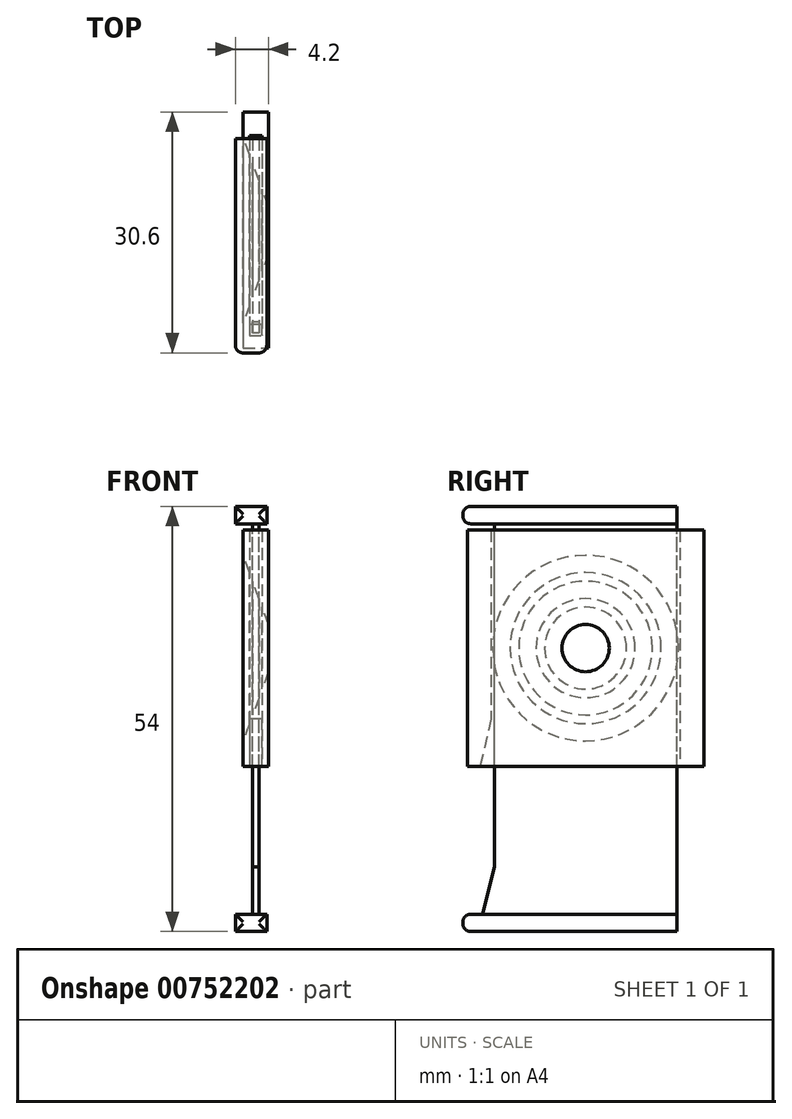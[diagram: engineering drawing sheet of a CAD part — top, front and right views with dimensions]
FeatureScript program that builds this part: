
annotation { "Feature Type Name" : "Feature", "Feature Type Description" : "" }
export const myFeature = defineFeature(function(context is Context, id is Id, definition is map)
    precondition{}
    {
        {
            var Q0;
            Q0=qCreatedBy(makeId("Top.planeOp"),FACE);
            var sketch = newSketch(context, id + "F0", { "sketchPlane" : qUnion([Q0])});
            skLineSegment(sketch, "E0.bottom", {"start": v(0, 15) * mm, "end": v(0.8, 15) * mm});
            skLineSegment(sketch, "E0.top", {"start": v(0, -15) * mm, "end": v(0.8, -15) * mm});
            skLineSegment(sketch, "E0.left", {"start": v(0, 15) * mm, "end": v(0, -15) * mm});
            skLineSegment(sketch, "E0.right", {"start": v(0.8, 15) * mm, "end": v(0.8, -15) * mm});
            skLineSegment(sketch, "E1.bottom", {"start": v(0.8, 15) * mm, "end": v(2.4, 15) * mm});
            skLineSegment(sketch, "E1.top", {"start": v(0.8, 12) * mm, "end": v(2.4, 12) * mm});
            skLineSegment(sketch, "E1.left", {"start": v(0.8, 15) * mm, "end": v(0.8, 12) * mm});
            skLineSegment(sketch, "E1.right", {"start": v(2.4, 15) * mm, "end": v(2.4, 12) * mm});
            skLineSegment(sketch, "E2.bottom", {"start": v(0.8, -15) * mm, "end": v(2.4, -15) * mm});
            skLineSegment(sketch, "E2.top", {"start": v(0.8, -12) * mm, "end": v(2.4, -12) * mm});
            skLineSegment(sketch, "E2.left", {"start": v(0.8, -15) * mm, "end": v(0.8, -12) * mm});
            skLineSegment(sketch, "E2.right", {"start": v(2.4, -15) * mm, "end": v(2.4, -12) * mm});
            skLineSegment(sketch, "E3.bottom", {"start": v(2.4, 15) * mm, "end": v(3.2, 15) * mm});
            skLineSegment(sketch, "E3.top", {"start": v(2.4, -15) * mm, "end": v(3.2, -15) * mm});
            skLineSegment(sketch, "E3.left", {"start": v(2.4, 15) * mm, "end": v(2.4, -15) * mm});
            skLineSegment(sketch, "E3.right", {"start": v(3.2, 15) * mm, "end": v(3.2, -15) * mm});
            skLineSegment(sketch, "E4.left", {"start": v(2.4, -15) * mm, "end": v(2.4, -15) * mm});
            skLineSegment(sketch, "E4.right", {"start": v(3.2, -15) * mm, "end": v(3.2, -15) * mm});
            skSolve(sketch);
        }
        {
            var Q0;
            Q0=makeQuery(id+"F0.imprint","IMPRINT",FACE,{"disambiguationData":[TD([[makeQuery(id+"F0.imprint","IMPRINT",EDGE,{"derivedFrom":sQuery(id+"F0.wireOp",EDGE,"E0.right")}),-1.0]])]});
            var Q1;
            {var subQ0=sQuery(id+"F0.wireOp",EDGE,"E1.bottom");Q1=makeQuery(id+"F0.imprint","IMPRINT",FACE,{"disambiguationData":[TD([[makeQuery(id+"F0.imprint","IMPRINT",EDGE,{"derivedFrom":subQ0}),-1.0]])]});}
            var Q2;
            {var subQ4=sQuery(id+"F0.wireOp",EDGE,"E3.bottom");Q2=makeQuery(id+"F0.imprint","IMPRINT",FACE,{"disambiguationData":[TD([[makeQuery(id+"F0.imprint","IMPRINT",EDGE,{"derivedFrom":subQ4}),-1.0]])]});}
            var Q3;
            {var subQ0=sQuery(id+"F0.wireOp",EDGE,"E2.bottom");Q3=makeQuery(id+"F0.imprint","IMPRINT",FACE,{"disambiguationData":[TD([[makeQuery(id+"F0.imprint","IMPRINT",EDGE,{"derivedFrom":subQ0}),1.0]])]});}
            var Q4;
            {var subQ0=sQuery(id+"F0.wireOp",EDGE,"E0.left");Q4=makeQuery(id+"F0.imprint","IMPRINT",FACE,{"disambiguationData":[TD([[makeQuery(id+"F0.imprint","IMPRINT",EDGE,{"derivedFrom":subQ0}),1.0]])]});}
            extrude(context, id + "F1", {"entities" : qUnion([Q0, Q1, Q2, Q3, Q4]), "endBound" : BoundingType.SYMMETRIC, "depth" : 30 * mm, "offsetDistance" : 25 * mm});
        }
        {
            var Q0;
            Q0=makeQuery(id+"F1.opExtrude","CAP_FACE",FACE,{"disambiguationData":[OSD([sQuery(id+"F0.wireOp",EDGE,"E0.bottom"),sQuery(id+"F0.wireOp",EDGE,"E0.top"),sQuery(id+"F0.wireOp",EDGE,"E0.left"),sQuery(id+"F0.wireOp",EDGE,"E0.right"),sQuery(id+"F0.wireOp",EDGE,"E1.bottom"),sQuery(id+"F0.wireOp",EDGE,"E1.top"),sQuery(id+"F0.wireOp",EDGE,"E2.bottom"),sQuery(id+"F0.wireOp",EDGE,"E2.top"),sQuery(id+"F0.wireOp",EDGE,"E3.bottom"),sQuery(id+"F0.wireOp",EDGE,"E3.left"),sQuery(id+"F0.wireOp",EDGE,"E3.right"),sQuery(id+"F0.wireOp",EDGE,"E3.top")])],"isStart":false});
            var sketch = newSketch(context, id + "F2", { "sketchPlane" : qUnion([Q0])});
            skLineSegment(sketch, "E5.bottom", {"start": v(1.2, 11.6) * mm, "end": v(2, 11.6) * mm});
            skLineSegment(sketch, "E5.top", {"start": v(1.2, -11.6) * mm, "end": v(2, -11.6) * mm});
            skLineSegment(sketch, "E5.left", {"start": v(1.2, 11.6) * mm, "end": v(1.2, -11.6) * mm});
            skLineSegment(sketch, "E5.right", {"start": v(2, 11.6) * mm, "end": v(2, -11.6) * mm});
            skSolve(sketch);
        }
        {
            var Q0;
            Q0=makeQuery(id+"F2.imprint","IMPRINT",FACE,{"disambiguationData":[TD([[makeQuery(id+"F2.imprint","IMPRINT",EDGE,{"derivedFrom":sQuery(id+"F2.wireOp",EDGE,"E5.bottom")}),-1.0]])]});
            extrude(context, id + "F3", {"entities" : qUnion([Q0]), "oppositeDirection" : true, "depth" : 50 * mm, "offsetDistance" : 25 * mm, "hasSecondDirection" : true, "secondDirectionOppositeDirection" : false, "secondDirectionDepth" : 2 * mm});
        }
        {
            var Q0;
            Q0=makeQuery(id+"F1.opExtrude","SWEPT_FACE",FACE,{"disambiguationData":[OSD([sQuery(id+"F0.wireOp",EDGE,"E3.right")])]});
            var sketch = newSketch(context, id + "F4", { "sketchPlane" : qUnion([Q0])});
            skCircle(sketch, "E6", {"center": v(0, 0) * mm, "radius": 3 * mm});
            skSolve(sketch);
        }
        {
            var Q0;
            Q0=qSketchRegion(id+"F4",true);
            extrude(context, id + "F5", {"entities" : qUnion([Q0]), "operationType" : NewBodyOperationType.REMOVE, "oppositeDirection" : true, "depth" : 25 * mm, "offsetDistance" : 25 * mm, "hasDraft" : true, "draftAngle" : 70 * degree});
        }
        {
            var Q0;
            Q0=makeQuery(id+"F3.opExtrude","SWEPT_FACE",FACE,{"disambiguationData":[OSD([sQuery(id+"F2.wireOp",EDGE,"E5.right")])]});
            var sketch = newSketch(context, id + "F6", { "sketchPlane" : qUnion([Q0])});
            skLineSegment(sketch, "E7.bottom", {"start": v(11.6, 17) * mm, "end": v(-15.6, 17) * mm});
            skLineSegment(sketch, "E7.top", {"start": v(11.6, 15.8) * mm, "end": v(-15.6, 15.8) * mm});
            skLineSegment(sketch, "E7.left", {"start": v(11.6, 17) * mm, "end": v(11.6, 15.8) * mm});
            skLineSegment(sketch, "E7.right", {"start": v(-15.6, 17) * mm, "end": v(-15.6, 15.8) * mm});
            skLineSegment(sketch, "E8.bottom", {"start": v(11.6, -35) * mm, "end": v(-15.6, -35) * mm});
            skLineSegment(sketch, "E8.top", {"start": v(11.6, -33.8) * mm, "end": v(-15.6, -33.8) * mm});
            skLineSegment(sketch, "E8.left", {"start": v(11.6, -35) * mm, "end": v(11.6, -33.8) * mm});
            skLineSegment(sketch, "E8.right", {"start": v(-15.6, -35) * mm, "end": v(-15.6, -33.8) * mm});
            skLineSegment(sketch, "E9.top", {"start": v(11.6, 18) * mm, "end": v(-15.6, 18) * mm});
            skLineSegment(sketch, "E9.left", {"start": v(11.6, 17) * mm, "end": v(11.6, 18) * mm});
            skLineSegment(sketch, "E9.right", {"start": v(-15.6, 17) * mm, "end": v(-15.6, 18) * mm});
            skLineSegment(sketch, "E10.top", {"start": v(11.6, -36) * mm, "end": v(-15.6, -36) * mm});
            skLineSegment(sketch, "E10.left", {"start": v(11.6, -35) * mm, "end": v(11.6, -36) * mm});
            skLineSegment(sketch, "E10.right", {"start": v(-15.6, -35) * mm, "end": v(-15.6, -36) * mm});
            skSolve(sketch);
        }
        {
            var Q0;
            Q0=qSketchRegion(id+"F6",true);
            extrude(context, id + "F7", {"entities" : qUnion([Q0]), "operationType" : NewBodyOperationType.ADD, "depth" : 1 * mm, "offsetDistance" : 25 * mm, "hasSecondDirection" : true, "secondDirectionOppositeDirection" : true, "secondDirectionDepth" : 3 * mm});
        }
        {
            var Q0;
            Q0=makeQuery(id+"F7.opExtrude","SWEPT_FACE",FACE,{"disambiguationData":[OSD([sQuery(id+"F6.wireOp",EDGE,"E8.right")])]});
            var Q1;
            Q1=makeQuery(id+"F7.opExtrude","SWEPT_FACE",FACE,{"disambiguationData":[OSD([sQuery(id+"F6.wireOp",EDGE,"E7.right")])]});
            fillet(context, id + "F8", {"entities" : qUnion([Q0, Q1]), "radius" : 1 * mm, "tangentPropagation" : true, "allowEdgeOverflow" : false});
        }
        {
            var Q0;
            Q0=makeQuery(id+"F7.boolean.opBoolean","INTERSECT",EDGE,{"derivedFrom":[makeQuery(id+"F3.opExtrude","SWEPT_FACE",FACE,{"disambiguationData":[OSD([sQuery(id+"F2.wireOp",EDGE,"E5.top")])]}),makeQuery(id+"F7.opExtrude","SWEPT_FACE",FACE,{"disambiguationData":[OSD([sQuery(id+"F6.wireOp",EDGE,"E8.top")])]})]});
            chamfer(context, id + "F9", {"entities" : qUnion([Q0]), "chamferType" : ChamferType.TWO_OFFSETS, "width1" : 6 * mm, "oppositeDirection" : false, "width2" : 1.5 * mm, "tangentPropagation" : true});
        }
        {
            var Q0;
            Q0=makeQuery(id+"F1.opExtrude","CAP_EDGE",EDGE,{"disambiguationData":[OSD([sQuery(id+"F0.wireOp",EDGE,"E2.top")])],"isStart":true});
            chamfer(context, id + "F10", {"entities" : qUnion([Q0]), "chamferType" : ChamferType.TWO_OFFSETS, "width1" : 1.4 * mm, "oppositeDirection" : false, "width2" : 6 * mm, "tangentPropagation" : true});
        }
    });
